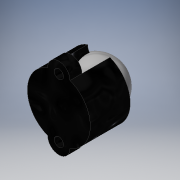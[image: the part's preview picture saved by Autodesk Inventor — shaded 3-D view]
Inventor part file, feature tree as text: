
AUTODESK INVENTOR PART (.ipt)
format: ipt  version: 2019 (Build 230136000, 136)  size: 173,056 bytes
history: native  units: mm
features: sketch x4, extrude x2, hole x1, revolve x1, projected_geometry x1
ambient origin geometry x8: Origin, YZ Plane, XZ Plane, XY Plane, X Axis, Y Axis, Z Axis, Center Point
bodies: Solid1 (feature_tree), Solid2 (feature_tree)
feature tree (9):
  extrude  "Extrusion1"  Depth=15.75mm
  extrude  "Extrusion2"  Depth=10.0mm TaperAngle=0.0deg
  hole  "Hole1"  [1 undecoded]
  revolve  "Revolution1"  [1 undecoded]
  sketch  "Sketch1"  dims[d0=14.732mm d1=15.75mm]
  sketch  "Sketch2"  dims[d2=5.59mm d3=10.0mm d4=0.0mm]
  sketch  "Sketch3"  dims[d5=7.0mm d6=0.0mm]
  sketch  "Sketch4"  dims[d7=2.3mm d8=6.0mm d9=6.0mm d10=2.0mm d11=90.0deg d12=8.0mm d13=20.594885mm d14=12.7mm d15=9.24mm d16=180.0deg]
  projected_geometry  "Projected Loop1"
note: 2 required parameter values undecoded (feature->parameter linkage not recoverable at this tier; creation-order binding heuristic only, values carry confidence <= 0.55)